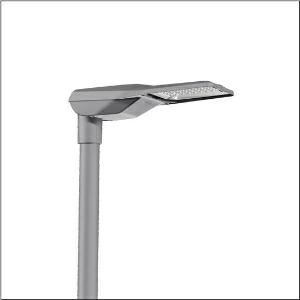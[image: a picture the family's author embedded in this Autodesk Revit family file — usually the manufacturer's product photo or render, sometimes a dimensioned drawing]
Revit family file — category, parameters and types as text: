
# Revit family: streetlight_sl_21_iq_mini___st1_5a_5xe2p41g08hb_3230
name_source: partatom
category: Lighting Fixtures
units: mm (PartAtom-declared; Revit-internal decimal feet)

## family parameters
Cut with Voids When Loaded = No
Host = Face
Light Source = No
Part Type = Normal
Room Calculation Point = No
Round Connector Dimension = Use Diameter
Shared = No

## types (1)
- --- (1 x LED, 9690 lm, 70.9 W, 4000K)
    Apparent Load = 71 VA
    CIE Flux Codes = 22 53 95 100 100
    Color Rendering = 70
    Color Temperature = 4000K
    Default Elevation = 1800 mm
    Description = Streetlight SL 21 iQ mini, mast luminaire, primary light control with lens, of PMMA, primary optical cover: cover, of toughened safety glass, transparent, light distribution: ST1.5a, light emission: direct distribution, primary light characteristic: asymmetric, installation type: post-top, side-entry, LED, High Power LED, rated luminous flux: 9.690lm, luminous efficacy: 137lm/W, light colour: 740, colour temperature: 4000K, control: Street-Remote, Auto-Match, Temp-Guard, Lumen-Switch, Night-Set, Smart-Wire, Light-Fading, Desk-Remote (wireless, voltage-free reading and setting of iQ features in the workshop via application-optimized NFC function/RFID function), optimised constant luminous flux control (CLO 2.0), presetting dimming linear, mains connection: 220..240V, AC, 50/60Hz, start of lifetime: 71W, end of service life: 75W, reduction: 31W, luminaire housing, of diecast aluminium, powder-coated, Siteco® metallic grey (DB 702S), corrosivity category C5 mid according to DIN EN ISO 12944, please order mast flange separately, inclination adjustable: 0°, 5°, 10°, 15°, sealing non-destructively replaceable, multi-level sealing system, length: 628mm, width: 235mm, height: 110mm, mast flange for spigot size: 42mm (side-entry): 5XC10008XM4, 60/48mm (side-entry/post-top): 5XC10108XM2, 76/60mm (side-entry/post-top): 5XC10108XM1, protection rating (complete): IP66, insulation class (complete): insulation class II (safety insulation), certification: CE, ENEC, ENEC+, VDE, impact resistance: IK09, permissible operating ambient temperature for outdoor applications: -40..+50°C, standard-compliant lighting for roads and squares, packaging unit: 1 piece

Light Distribution: ST1.5a
    Height = 110 mm
    Lamp = 1 x LED
    Lamp Light Flux = 9690 lm
    Lamp Power = 70.9 W
    Lamp count = 1
    Length = 625 mm
    Luminous efficacy = 137 lm/W
    Manufacturer = Siteco
    ModVariant = No
    Model = 5XE2P41G08HB
    Number of Poles = 1
    OnlyDefault = Yes
    Power Factor = 1
    Product Name = Streetlight SL 21 iQ mini | ST1.5a
    Product group = mast luminaire | pylon top
    ProductGroupID = 6100
    Protection Class = Protection class II
    Protection Degree = IP 66
    RLX_Detail_Level = 1
    RLX_Emergency_Light_Flux = 0 lm
    RLX_Emergency_Type = 0
    RLX_Emergency_Type_DB = No
    RlxData = <blob elided: 95905 chars, md5=a127c480>
    Socket = socket
    Standby Power = 0 W
    System Light Flux = 9690 lm
    System Power = 71 W
    Type Comments = factory setting: luminous flux: 100 % | dim-lin: 254 | 711 mA
    Type Image = l_1003519.jpg
    URL = http://relux.com
    VarID = @adj_107169
    Voltage = 0 V
    Weight = 0.00 kg
    Width = 234 mm

## geometry (parser evidence)
native form markers: Blend x4, Sweep x10
no freeform markers — native parametric forms only
